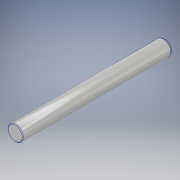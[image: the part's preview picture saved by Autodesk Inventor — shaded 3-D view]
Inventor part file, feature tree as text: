
AUTODESK INVENTOR PART (.ipt)
format: ipt  version: 2019.4 (Build 234330000, 330)  size: 137,216 bytes
history: native  units: mm
features: extrude x2, chamfer x2, sketch x2, fillet x1
ambient origin geometry x8: Origin, YZ Plane, XZ Plane, XY Plane, X Axis, Y Axis, Z Axis, Center Point
bodies: Solide1 (feature_tree)
feature tree (7):
  extrude  "Extrusion1"  Depth=5.0mm
  chamfer  "Chanfrein1"  Distance=49.0mm
  chamfer  "Chanfrein2"  Distance=0.2mm Angle=45.0deg
  extrude  "Extrusion2"  Depth=0.3mm TaperAngle=60.0deg
  fillet  "Congé1"  Radius=4.5mm
  sketch  "Esquisse1"
  sketch  "Esquisse2"
